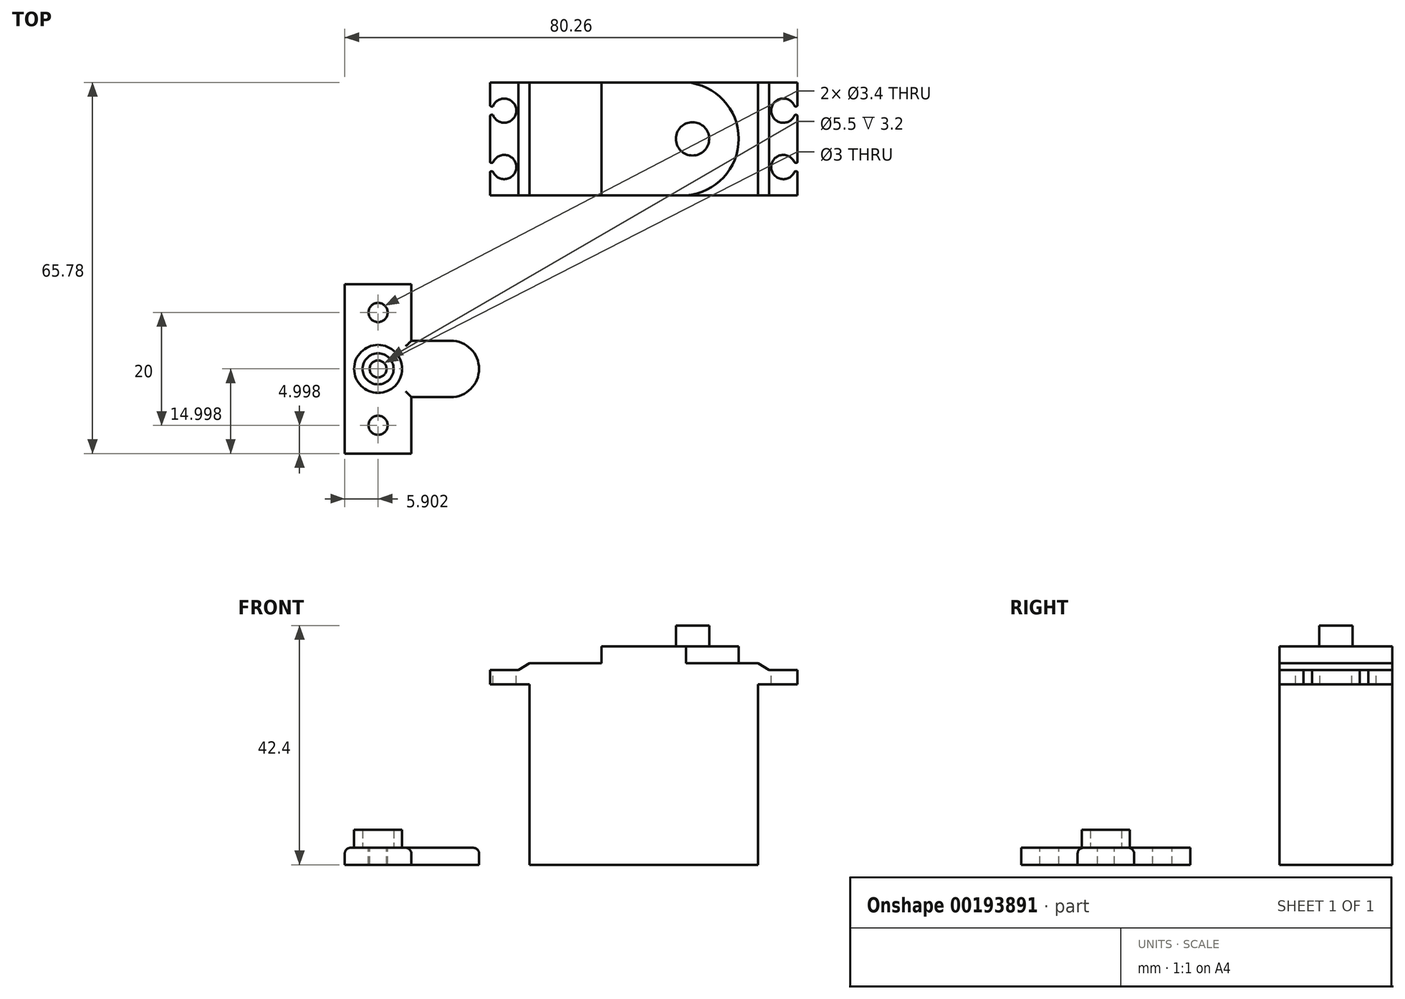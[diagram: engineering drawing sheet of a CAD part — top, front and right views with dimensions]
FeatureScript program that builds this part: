
annotation { "Feature Type Name" : "Feature", "Feature Type Description" : "" }
export const myFeature = defineFeature(function(context is Context, id is Id, definition is map)
    precondition{}
    {
        {
            var Q0;
            Q0=qCreatedBy(makeId("Top.planeOp"),FACE);
            var sketch = newSketch(context, id + "F0", { "sketchPlane" : qUnion([Q0])});
            skLineSegment(sketch, "E0.bottom", {"start": v(20.25, -10) * mm, "end": v(-20.25, -10) * mm});
            skLineSegment(sketch, "E0.top", {"start": v(20.25, 10) * mm, "end": v(-20.25, 10) * mm});
            skLineSegment(sketch, "E0.left", {"start": v(20.25, -10) * mm, "end": v(20.25, 10) * mm});
            skLineSegment(sketch, "E0.right", {"start": v(-20.25, -10) * mm, "end": v(-20.25, 10) * mm});
            skPoint(sketch, "E0.middle", {"position": v(0, 0) * mm});
            skSolve(sketch);
        }
        {
            var Q0;
            Q0 = qSketchRegion(id + "F0", true);
            extrude(context, id + "F1", {"entities" : qUnion([Q0]), "depth" : 32 * mm});
        }
        {
            var Q0;
            Q0=makeQuery(id+"F1.opExtrude","CAP_FACE",FACE,{"disambiguationData":[OSD([sQuery(id+"F0.wireOp",EDGE,"E0.bottom"),sQuery(id+"F0.wireOp",EDGE,"E0.top"),sQuery(id+"F0.wireOp",EDGE,"E0.left"),sQuery(id+"F0.wireOp",EDGE,"E0.right")])],"isStart":false});
            var sketch = newSketch(context, id + "F2", { "sketchPlane" : qUnion([Q0])});
            skLineSegment(sketch, "E1.bottom", {"start": v(-27.25, -10) * mm, "end": v(27.25, -10) * mm});
            skLineSegment(sketch, "E1.top", {"start": v(-27.25, 10) * mm, "end": v(27.25, 10) * mm});
            skLineSegment(sketch, "E1.left", {"start": v(-27.25, -10) * mm, "end": v(-27.25, 10) * mm});
            skLineSegment(sketch, "E1.right", {"start": v(27.25, -10) * mm, "end": v(27.25, 10) * mm});
            skPoint(sketch, "E1.middle", {"position": v(0, 0) * mm});
            skSolve(sketch);
        }
        {
            var Q0;
            Q0 = qSketchRegion(id + "F2", true);
            extrude(context, id + "F3", {"entities" : qUnion([Q0]), "operationType" : NewBodyOperationType.ADD, "depth" : 3.7 * mm});
        }
        {
            var Q0;
            Q0=makeQuery(id+"F3.boolean.opBoolean","MERGE",FACE,{"derivedFrom":[makeQuery(id+"F1.opExtrude","SWEPT_FACE",FACE,{"disambiguationData":[OSD([sQuery(id+"F0.wireOp",EDGE,"E0.bottom")])]}),makeQuery(id+"F3.opExtrude","SWEPT_FACE",FACE,{"disambiguationData":[OSD([sQuery(id+"F2.wireOp",EDGE,"E1.bottom")])]})]});
            var sketch = newSketch(context, id + "F4", { "sketchPlane" : qUnion([Q0])});
            skLineSegment(sketch, "E2.0", {"start": v(-27.25, 35.7) * mm, "end": v(27.25, 35.7) * mm});
            skPoint(sketch, "E3.0", {"position": v(23.75, 32) * mm});
            skLineSegment(sketch, "E4.0", {"start": v(20.25, 32) * mm, "end": v(27.25, 32) * mm});
            skLineSegment(sketch, "E5", {"start": v(27.25, 35.7) * mm, "end": v(27.25, 34.5) * mm});
            skLineSegment(sketch, "E6", {"start": v(27.25, 34.5) * mm, "end": v(22.25, 34.5) * mm});
            skLineSegment(sketch, "E7", {"start": v(22.25, 34.5) * mm, "end": v(20.25, 35.7) * mm});
            skLineSegment(sketch, "E8", {"start": v(20.25, 35.7) * mm, "end": v(27.25, 35.7) * mm});
            skLineSegment(sketch, "E9.MirrorCS", {"start": v(-27.25, 35.7) * mm, "end": v(-27.25, 34.5) * mm});
            skLineSegment(sketch, "E10.MirrorCS", {"start": v(-20.25, 35.7) * mm, "end": v(-27.25, 35.7) * mm});
            skLineSegment(sketch, "E11.MirrorCS", {"start": v(-27.25, 34.5) * mm, "end": v(-22.25, 34.5) * mm});
            skLineSegment(sketch, "E12.MirrorCS", {"start": v(-22.25, 34.5) * mm, "end": v(-20.25, 35.7) * mm});
            skSolve(sketch);
        }
        {
            var Q0;
            Q0 = qSketchRegion(id + "F4", true);
            extrude(context, id + "F5", {"entities" : qUnion([Q0]), "operationType" : NewBodyOperationType.REMOVE, "endBound" : BoundingType.THROUGH_ALL, "oppositeDirection" : true, "depth" : 25 * mm});
        }
        {
            var Q0;
            Q0=makeQuery(id+"F5.boolean.opBoolean","COPY",FACE,{"derivedFrom":makeQuery(id+"F5.opExtrude","SWEPT_FACE",FACE,{"disambiguationData":[OSD([sQuery(id+"F4.wireOp",EDGE,"E6")])]})});
            var sketch = newSketch(context, id + "F6", { "sketchPlane" : qUnion([Q0])});
            skCircle(sketch, "E13", {"center": v(24.75, 5) * mm, "radius": 2.15 * mm});
            skCircle(sketch, "E14", {"center": v(24.75, -5) * mm, "radius": 2.15 * mm});
            skLineSegment(sketch, "E15.0", {"start": v(27.25, 10) * mm, "end": v(27.25, -10) * mm});
            skCircle(sketch, "E16.MirrorC", {"center": v(-24.75, 5) * mm, "radius": 2.15 * mm});
            skCircle(sketch, "E17.MirrorC", {"center": v(-24.75, -5) * mm, "radius": 2.15 * mm});
            skSolve(sketch);
        }
        {
            var Q0;
            Q0 = qSketchRegion(id + "F6", true);
            extrude(context, id + "F7", {"entities" : qUnion([Q0]), "operationType" : NewBodyOperationType.REMOVE, "endBound" : BoundingType.THROUGH_ALL, "oppositeDirection" : true, "depth" : 25 * mm});
        }
        {
            var Q0;
            Q0=makeQuery(id+"F5.boolean.opBoolean","COPY",FACE,{"derivedFrom":makeQuery(id+"F5.opExtrude","SWEPT_FACE",FACE,{"disambiguationData":[OSD([sQuery(id+"F4.wireOp",EDGE,"E11.MirrorCS")])]})});
            var sketch = newSketch(context, id + "F8", { "sketchPlane" : qUnion([Q0])});
            skLineSegment(sketch, "E18.bottom", {"start": v(-25.35, 4.25) * mm, "end": v(-31.35, 4.25) * mm});
            skLineSegment(sketch, "E18.top", {"start": v(-25.35, 5.75) * mm, "end": v(-31.35, 5.75) * mm});
            skLineSegment(sketch, "E18.left", {"start": v(-25.35, 4.25) * mm, "end": v(-25.35, 5.75) * mm});
            skLineSegment(sketch, "E18.right", {"start": v(-31.35, 4.25) * mm, "end": v(-31.35, 5.75) * mm});
            skPoint(sketch, "E18.middle", {"position": v(-28.35, 5) * mm});
            skCircle(sketch, "E19.0", {"center": v(-24.75, 5) * mm, "radius": 2.15 * mm});
            skLineSegment(sketch, "E20.MirrorCS", {"start": v(-25.35, -4.25) * mm, "end": v(-31.35, -4.25) * mm});
            skLineSegment(sketch, "E21.MirrorCS", {"start": v(-31.35, -4.25) * mm, "end": v(-31.35, -5.75) * mm});
            skLineSegment(sketch, "E22.MirrorCS", {"start": v(-25.35, -5.75) * mm, "end": v(-31.35, -5.75) * mm});
            skLineSegment(sketch, "E23.MirrorCS", {"start": v(-25.35, -4.25) * mm, "end": v(-25.35, -5.75) * mm});
            skLineSegment(sketch, "E24.MirrorCS", {"start": v(25.35, 4.25) * mm, "end": v(25.35, 5.75) * mm});
            skLineSegment(sketch, "E25.MirrorCS", {"start": v(31.35, 4.25) * mm, "end": v(31.35, 5.75) * mm});
            skLineSegment(sketch, "E26.MirrorCS", {"start": v(31.35, -4.25) * mm, "end": v(31.35, -5.75) * mm});
            skLineSegment(sketch, "E27.MirrorCS", {"start": v(25.35, -4.25) * mm, "end": v(25.35, -5.75) * mm});
            skLineSegment(sketch, "E28.MirrorCS", {"start": v(25.35, 5.75) * mm, "end": v(31.35, 5.75) * mm});
            skLineSegment(sketch, "E29.MirrorCS", {"start": v(25.35, 4.25) * mm, "end": v(31.35, 4.25) * mm});
            skPoint(sketch, "E30.MirrorP", {"position": v(28.35, 5) * mm});
            skLineSegment(sketch, "E31.MirrorCS", {"start": v(25.35, -4.25) * mm, "end": v(31.35, -4.25) * mm});
            skLineSegment(sketch, "E32.MirrorCS", {"start": v(25.35, -5.75) * mm, "end": v(31.35, -5.75) * mm});
            skSolve(sketch);
        }
        {
            var Q0;
            Q0 = qSketchRegion(id + "F8", true);
            extrude(context, id + "F9", {"entities" : qUnion([Q0]), "operationType" : NewBodyOperationType.REMOVE, "endBound" : BoundingType.THROUGH_ALL, "oppositeDirection" : true, "depth" : 25 * mm});
        }
        {
            var Q0;
            Q0=makeQuery(id+"F9.boolean.opBoolean","INTERSECT",EDGE,{"derivedFrom":[makeQuery(id+"F3.opExtrude","SWEPT_FACE",FACE,{"disambiguationData":[OSD([sQuery(id+"F2.wireOp",EDGE,"E1.right")])]}),makeQuery(id+"F9.opExtrude","SWEPT_FACE",FACE,{"disambiguationData":[OSD([sQuery(id+"F8.wireOp",EDGE,"E28.MirrorCS")])]})]});
            var Q1;
            Q1=makeQuery(id+"F9.boolean.opBoolean","INTERSECT",EDGE,{"derivedFrom":[makeQuery(id+"F7.boolean.opBoolean","COPY",FACE,{"derivedFrom":makeQuery(id+"F7.opExtrude","SWEPT_FACE",FACE,{"disambiguationData":[OSD([sQuery(id+"F6.wireOp",EDGE,"E13")])]})}),makeQuery(id+"F9.opExtrude","SWEPT_FACE",FACE,{"disambiguationData":[OSD([sQuery(id+"F8.wireOp",EDGE,"E28.MirrorCS")])]})]});
            var Q2;
            Q2=makeQuery(id+"F9.boolean.opBoolean","INTERSECT",EDGE,{"derivedFrom":[makeQuery(id+"F7.boolean.opBoolean","COPY",FACE,{"derivedFrom":makeQuery(id+"F7.opExtrude","SWEPT_FACE",FACE,{"disambiguationData":[OSD([sQuery(id+"F6.wireOp",EDGE,"E13")])]})}),makeQuery(id+"F9.opExtrude","SWEPT_FACE",FACE,{"disambiguationData":[OSD([sQuery(id+"F8.wireOp",EDGE,"E29.MirrorCS")])]})]});
            var Q3;
            Q3=makeQuery(id+"F9.boolean.opBoolean","INTERSECT",EDGE,{"derivedFrom":[makeQuery(id+"F3.opExtrude","SWEPT_FACE",FACE,{"disambiguationData":[OSD([sQuery(id+"F2.wireOp",EDGE,"E1.right")])]}),makeQuery(id+"F9.opExtrude","SWEPT_FACE",FACE,{"disambiguationData":[OSD([sQuery(id+"F8.wireOp",EDGE,"E29.MirrorCS")])]})]});
            var Q4;
            Q4=makeQuery(id+"F9.boolean.opBoolean","INTERSECT",EDGE,{"derivedFrom":[makeQuery(id+"F3.opExtrude","SWEPT_FACE",FACE,{"disambiguationData":[OSD([sQuery(id+"F2.wireOp",EDGE,"E1.right")])]}),makeQuery(id+"F9.opExtrude","SWEPT_FACE",FACE,{"disambiguationData":[OSD([sQuery(id+"F8.wireOp",EDGE,"E31.MirrorCS")])]})]});
            var Q5;
            Q5=makeQuery(id+"F9.boolean.opBoolean","INTERSECT",EDGE,{"derivedFrom":[makeQuery(id+"F7.boolean.opBoolean","COPY",FACE,{"derivedFrom":makeQuery(id+"F7.opExtrude","SWEPT_FACE",FACE,{"disambiguationData":[OSD([sQuery(id+"F6.wireOp",EDGE,"E14")])]})}),makeQuery(id+"F9.opExtrude","SWEPT_FACE",FACE,{"disambiguationData":[OSD([sQuery(id+"F8.wireOp",EDGE,"E31.MirrorCS")])]})]});
            var Q6;
            Q6=makeQuery(id+"F9.boolean.opBoolean","INTERSECT",EDGE,{"derivedFrom":[makeQuery(id+"F7.boolean.opBoolean","COPY",FACE,{"derivedFrom":makeQuery(id+"F7.opExtrude","SWEPT_FACE",FACE,{"disambiguationData":[OSD([sQuery(id+"F6.wireOp",EDGE,"E14")])]})}),makeQuery(id+"F9.opExtrude","SWEPT_FACE",FACE,{"disambiguationData":[OSD([sQuery(id+"F8.wireOp",EDGE,"E32.MirrorCS")])]})]});
            var Q7;
            Q7=makeQuery(id+"F9.boolean.opBoolean","INTERSECT",EDGE,{"derivedFrom":[makeQuery(id+"F3.opExtrude","SWEPT_FACE",FACE,{"disambiguationData":[OSD([sQuery(id+"F2.wireOp",EDGE,"E1.right")])]}),makeQuery(id+"F9.opExtrude","SWEPT_FACE",FACE,{"disambiguationData":[OSD([sQuery(id+"F8.wireOp",EDGE,"E32.MirrorCS")])]})]});
            fillet(context, id + "F10", {"entities" : qUnion([Q0, Q1, Q2, Q3, Q4, Q5, Q6, Q7]), "radius" : 0.2 * mm, "tangentPropagation" : true, "allowEdgeOverflow" : false});
        }
        {
            var Q0;
            Q0=makeQuery(id+"F9.boolean.opBoolean","COPY",EDGE,{"derivedFrom":makeQuery(id+"F9.opExtrude","SWEPT_EDGE",EDGE,{"disambiguationData":[OSD([sQuery(id+"F8.wireOp",EDGE,"E18.bottom"),sQuery(id+"F8.wireOp",EDGE,"E19.0")])]})});
            var Q1;
            Q1=makeQuery(id+"F9.boolean.opBoolean","INTERSECT",EDGE,{"derivedFrom":[makeQuery(id+"F3.opExtrude","SWEPT_FACE",FACE,{"disambiguationData":[OSD([sQuery(id+"F2.wireOp",EDGE,"E1.left")])]}),makeQuery(id+"F9.opExtrude","SWEPT_FACE",FACE,{"disambiguationData":[OSD([sQuery(id+"F8.wireOp",EDGE,"E18.bottom")])]})]});
            var Q2;
            Q2=makeQuery(id+"F9.boolean.opBoolean","INTERSECT",EDGE,{"derivedFrom":[makeQuery(id+"F3.opExtrude","SWEPT_FACE",FACE,{"disambiguationData":[OSD([sQuery(id+"F2.wireOp",EDGE,"E1.left")])]}),makeQuery(id+"F9.opExtrude","SWEPT_FACE",FACE,{"disambiguationData":[OSD([sQuery(id+"F8.wireOp",EDGE,"E22.MirrorCS")])]})]});
            var Q3;
            Q3=makeQuery(id+"F9.boolean.opBoolean","INTERSECT",EDGE,{"derivedFrom":[makeQuery(id+"F7.boolean.opBoolean","COPY",FACE,{"derivedFrom":makeQuery(id+"F7.opExtrude","SWEPT_FACE",FACE,{"disambiguationData":[OSD([sQuery(id+"F6.wireOp",EDGE,"E17.MirrorC")])]})}),makeQuery(id+"F9.opExtrude","SWEPT_FACE",FACE,{"disambiguationData":[OSD([sQuery(id+"F8.wireOp",EDGE,"E22.MirrorCS")])]})]});
            var Q4;
            Q4=makeQuery(id+"F9.boolean.opBoolean","INTERSECT",EDGE,{"derivedFrom":[makeQuery(id+"F3.opExtrude","SWEPT_FACE",FACE,{"disambiguationData":[OSD([sQuery(id+"F2.wireOp",EDGE,"E1.left")])]}),makeQuery(id+"F9.opExtrude","SWEPT_FACE",FACE,{"disambiguationData":[OSD([sQuery(id+"F8.wireOp",EDGE,"E18.top")])]})]});
            var Q5;
            Q5=makeQuery(id+"F9.boolean.opBoolean","INTERSECT",EDGE,{"derivedFrom":[makeQuery(id+"F3.opExtrude","SWEPT_FACE",FACE,{"disambiguationData":[OSD([sQuery(id+"F2.wireOp",EDGE,"E1.left")])]}),makeQuery(id+"F9.opExtrude","SWEPT_FACE",FACE,{"disambiguationData":[OSD([sQuery(id+"F8.wireOp",EDGE,"E20.MirrorCS")])]})]});
            var Q6;
            Q6=makeQuery(id+"F9.boolean.opBoolean","INTERSECT",EDGE,{"derivedFrom":[makeQuery(id+"F7.boolean.opBoolean","COPY",FACE,{"derivedFrom":makeQuery(id+"F7.opExtrude","SWEPT_FACE",FACE,{"disambiguationData":[OSD([sQuery(id+"F6.wireOp",EDGE,"E17.MirrorC")])]})}),makeQuery(id+"F9.opExtrude","SWEPT_FACE",FACE,{"disambiguationData":[OSD([sQuery(id+"F8.wireOp",EDGE,"E20.MirrorCS")])]})]});
            fillet(context, id + "F11", {"entities" : qUnion([Q0, Q1, Q2, Q3, Q4, Q5, Q6]), "radius" : 0.2 * mm, "tangentPropagation" : true, "allowEdgeOverflow" : false});
        }
        {
            var Q0;
            Q0=makeQuery(id+"F3.opExtrude","CAP_FACE",FACE,{"disambiguationData":[OSD([sQuery(id+"F2.wireOp",EDGE,"E1.bottom"),sQuery(id+"F2.wireOp",EDGE,"E1.top"),sQuery(id+"F2.wireOp",EDGE,"E1.left"),sQuery(id+"F2.wireOp",EDGE,"E1.right")])],"isStart":false});
            var sketch = newSketch(context, id + "F12", { "sketchPlane" : qUnion([Q0])});
            skLineSegment(sketch, "E33", {"start": v(7.51, 10) * mm, "end": v(-7.49, 10) * mm});
            skLineSegment(sketch, "E34", {"start": v(-7.49, 10) * mm, "end": v(-7.49, -10) * mm});
            skLineSegment(sketch, "E35", {"start": v(-7.49, -10) * mm, "end": v(7.51, -10) * mm});
            skLineSegment(sketch, "E36.0", {"start": v(-20.25, 10) * mm, "end": v(20.25, 10) * mm});
            skArc(sketch, "E37", {"start": v(7.51, -10) * mm, "mid": v(16.83, 0) * mm, "end": v(7.51, 10) * mm});
            skSolve(sketch);
        }
        {
            var Q0;
            Q0 = qSketchRegion(id + "F12", true);
            extrude(context, id + "F13", {"entities" : qUnion([Q0]), "operationType" : NewBodyOperationType.ADD, "depth" : 3 * mm});
        }
        {
            var Q0;
            Q0=makeQuery(id+"F13.opExtrude","CAP_FACE",FACE,{"disambiguationData":[OSD([sQuery(id+"F12.wireOp",EDGE,"E34"),sQuery(id+"F12.wireOp",EDGE,"E35"),sQuery(id+"F12.wireOp",EDGE,"E36.0"),sQuery(id+"F12.wireOp",EDGE,"E37")])],"isStart":false});
            var sketch = newSketch(context, id + "F14", { "sketchPlane" : qUnion([Q0])});
            skCircle(sketch, "E38", {"center": v(8.65, 0) * mm, "radius": 2.95 * mm});
            skLineSegment(sketch, "E39.0", {"start": v(20.25, 10) * mm, "end": v(20.25, -10) * mm});
            skSolve(sketch);
        }
        {
            var Q0;
            Q0 = qSketchRegion(id + "F14", true);
            extrude(context, id + "F15", {"entities" : qUnion([Q0]), "operationType" : NewBodyOperationType.ADD, "depth" : 3.7 * mm});
        }
        {
            var Q0;
            Q0=qCreatedBy(makeId("Top.planeOp"),FACE);
            var sketch = newSketch(context, id + "F16", { "sketchPlane" : qUnion([Q0])});
            skLineSegment(sketch, "E40", {"start": v(-53, -25.78) * mm, "end": v(-53, -55.78) * mm});
            skLineSegment(sketch, "E41", {"start": v(-53, -25.78) * mm, "end": v(-41.2, -25.78) * mm});
            skLineSegment(sketch, "E42", {"start": v(-41.2, -25.78) * mm, "end": v(-41.2, -35.78) * mm});
            skLineSegment(sketch, "E43", {"start": v(-41.2, -35.78) * mm, "end": v(-34.2, -35.78) * mm});
            skLineSegment(sketch, "E44", {"start": v(-53, -55.78) * mm, "end": v(-41.2, -55.78) * mm});
            skLineSegment(sketch, "E45", {"start": v(-41.2, -55.78) * mm, "end": v(-41.2, -45.78) * mm});
            skLineSegment(sketch, "E46", {"start": v(-41.2, -45.78) * mm, "end": v(-34.2, -45.78) * mm});
            skArc(sketch, "E47", {"start": v(-34.2, -45.78) * mm, "mid": v(-29.2, -40.78) * mm, "end": v(-34.2, -35.78) * mm});
            skSolve(sketch);
        }
        {
            var Q0;
            Q0 = qSketchRegion(id + "F16", true);
            extrude(context, id + "F17", {"entities" : qUnion([Q0]), "depth" : 3 * mm});
        }
        {
            var Q0;
            Q0=makeQuery(id+"F17.opExtrude","CAP_EDGE",EDGE,{"disambiguationData":[OSD([sQuery(id+"F16.wireOp",EDGE,"E40")])],"isStart":false});
            var Q1;
            Q1=makeQuery(id+"F17.opExtrude","CAP_EDGE",EDGE,{"disambiguationData":[OSD([sQuery(id+"F16.wireOp",EDGE,"E43")])],"isStart":false});
            var Q2;
            Q2=makeQuery(id+"F17.opExtrude","CAP_EDGE",EDGE,{"disambiguationData":[OSD([sQuery(id+"F16.wireOp",EDGE,"E42")])],"isStart":false});
            var Q3;
            Q3=makeQuery(id+"F17.opExtrude","CAP_EDGE",EDGE,{"disambiguationData":[OSD([sQuery(id+"F16.wireOp",EDGE,"E45")])],"isStart":false});
            fillet(context, id + "F18", {"entities" : qUnion([Q0, Q1, Q2, Q3]), "radius" : 1 * mm, "tangentPropagation" : true, "allowEdgeOverflow" : false});
        }
        {
            var Q0;
            Q0=makeQuery(id+"F17.opExtrude","CAP_FACE",FACE,{"disambiguationData":[OSD([sQuery(id+"F16.wireOp",EDGE,"E40"),sQuery(id+"F16.wireOp",EDGE,"E41"),sQuery(id+"F16.wireOp",EDGE,"E42"),sQuery(id+"F16.wireOp",EDGE,"E43"),sQuery(id+"F16.wireOp",EDGE,"E44"),sQuery(id+"F16.wireOp",EDGE,"E45"),sQuery(id+"F16.wireOp",EDGE,"E46"),sQuery(id+"F16.wireOp",EDGE,"E47")])],"isStart":false});
            var sketch = newSketch(context, id + "F19", { "sketchPlane" : qUnion([Q0])});
            skCircle(sketch, "E48", {"center": v(-47.1, -40.78) * mm, "radius": 2.75 * mm});
            skPoint(sketch, "E48.centerSnap0", {"position": v(-52, -40.78) * mm});
            skPoint(sketch, "E48.centerSnap1", {"position": v(-47.1, -25.78) * mm});
            skCircle(sketch, "E49.0", {"center": v(-47.1, -40.78) * mm, "radius": 4.25 * mm});
            skSolve(sketch);
        }
        {
            var Q0;
            Q0 = qSketchRegion(id + "F19", true);
            extrude(context, id + "F20", {"entities" : qUnion([Q0]), "operationType" : NewBodyOperationType.ADD, "depth" : 3.2 * mm});
        }
        {
            var Q0;
            {var subQ0=sQuery(id+"F16.wireOp",EDGE,"E42");var subQ1=sQuery(id+"F16.wireOp",EDGE,"E40");var subQ2=sQuery(id+"F16.wireOp",EDGE,"E44");var subQ3=sQuery(id+"F16.wireOp",EDGE,"E47");var subQ4=sQuery(id+"F16.wireOp",EDGE,"E41");var subQ5=sQuery(id+"F16.wireOp",EDGE,"E45");var subQ6=sQuery(id+"F16.wireOp",EDGE,"E43");var subQ7=sQuery(id+"F16.wireOp",EDGE,"E46");Q0=makeQuery(id+"F20.boolean.opBoolean","SPLIT",FACE,{"disambiguationData":[TD([makeQuery(id+"F17.opExtrude","SWEPT_FACE",FACE,{"disambiguationData":[OSD([subQ4])]})])],"derivedFrom":makeQuery(id+"F17.opExtrude","CAP_FACE",FACE,{"disambiguationData":[OSD([subQ1,subQ4,subQ0,subQ6,subQ2,subQ5,subQ7,subQ3])],"isStart":false})});}
            var sketch = newSketch(context, id + "F21", { "sketchPlane" : qUnion([Q0])});
            skCircle(sketch, "E50.0", {"center": v(-47.1, -40.78) * mm, "radius": 2.75 * mm, "construction": true});
            skCircle(sketch, "E51", {"center": v(-47.1, -40.78) * mm, "radius": 1.5 * mm});
            skSolve(sketch);
        }
        {
            var Q0;
            Q0 = qSketchRegion(id + "F21", true);
            extrude(context, id + "F22", {"entities" : qUnion([Q0]), "operationType" : NewBodyOperationType.REMOVE, "endBound" : BoundingType.THROUGH_ALL, "oppositeDirection" : true, "depth" : 25 * mm});
        }
        {
            var Q0;
            {var subQ0=sQuery(id+"F16.wireOp",EDGE,"E42");var subQ1=sQuery(id+"F16.wireOp",EDGE,"E40");var subQ2=sQuery(id+"F16.wireOp",EDGE,"E44");var subQ3=sQuery(id+"F16.wireOp",EDGE,"E47");var subQ4=sQuery(id+"F16.wireOp",EDGE,"E41");var subQ5=sQuery(id+"F16.wireOp",EDGE,"E45");var subQ6=sQuery(id+"F16.wireOp",EDGE,"E43");var subQ7=sQuery(id+"F16.wireOp",EDGE,"E46");Q0=makeQuery(id+"F20.boolean.opBoolean","SPLIT",FACE,{"disambiguationData":[TD([makeQuery(id+"F17.opExtrude","SWEPT_FACE",FACE,{"disambiguationData":[OSD([subQ4])]})])],"derivedFrom":makeQuery(id+"F17.opExtrude","CAP_FACE",FACE,{"disambiguationData":[OSD([subQ1,subQ4,subQ0,subQ6,subQ2,subQ5,subQ7,subQ3])],"isStart":false})});}
            var sketch = newSketch(context, id + "F23", { "sketchPlane" : qUnion([Q0])});
            skCircle(sketch, "E52", {"center": v(-47.1, -30.78) * mm, "radius": 1.7 * mm});
            skPoint(sketch, "E52.centerSnap0", {"position": v(-47.1, -25.78) * mm});
            skCircle(sketch, "E53", {"center": v(-47.1, -50.78) * mm, "radius": 1.7 * mm});
            skCircle(sketch, "E54.0", {"center": v(-47.1, -40.78) * mm, "radius": 1.5 * mm, "construction": true});
            skLineSegment(sketch, "E55", {"start": v(-47.1, -40.78) * mm, "end": v(-61.17, -40.78) * mm, "construction": true});
            skSolve(sketch);
        }
        {
            var Q0;
            Q0 = qSketchRegion(id + "F23", true);
            extrude(context, id + "F24", {"entities" : qUnion([Q0]), "operationType" : NewBodyOperationType.REMOVE, "endBound" : BoundingType.THROUGH_ALL, "oppositeDirection" : true, "depth" : 25 * mm});
        }
    });
